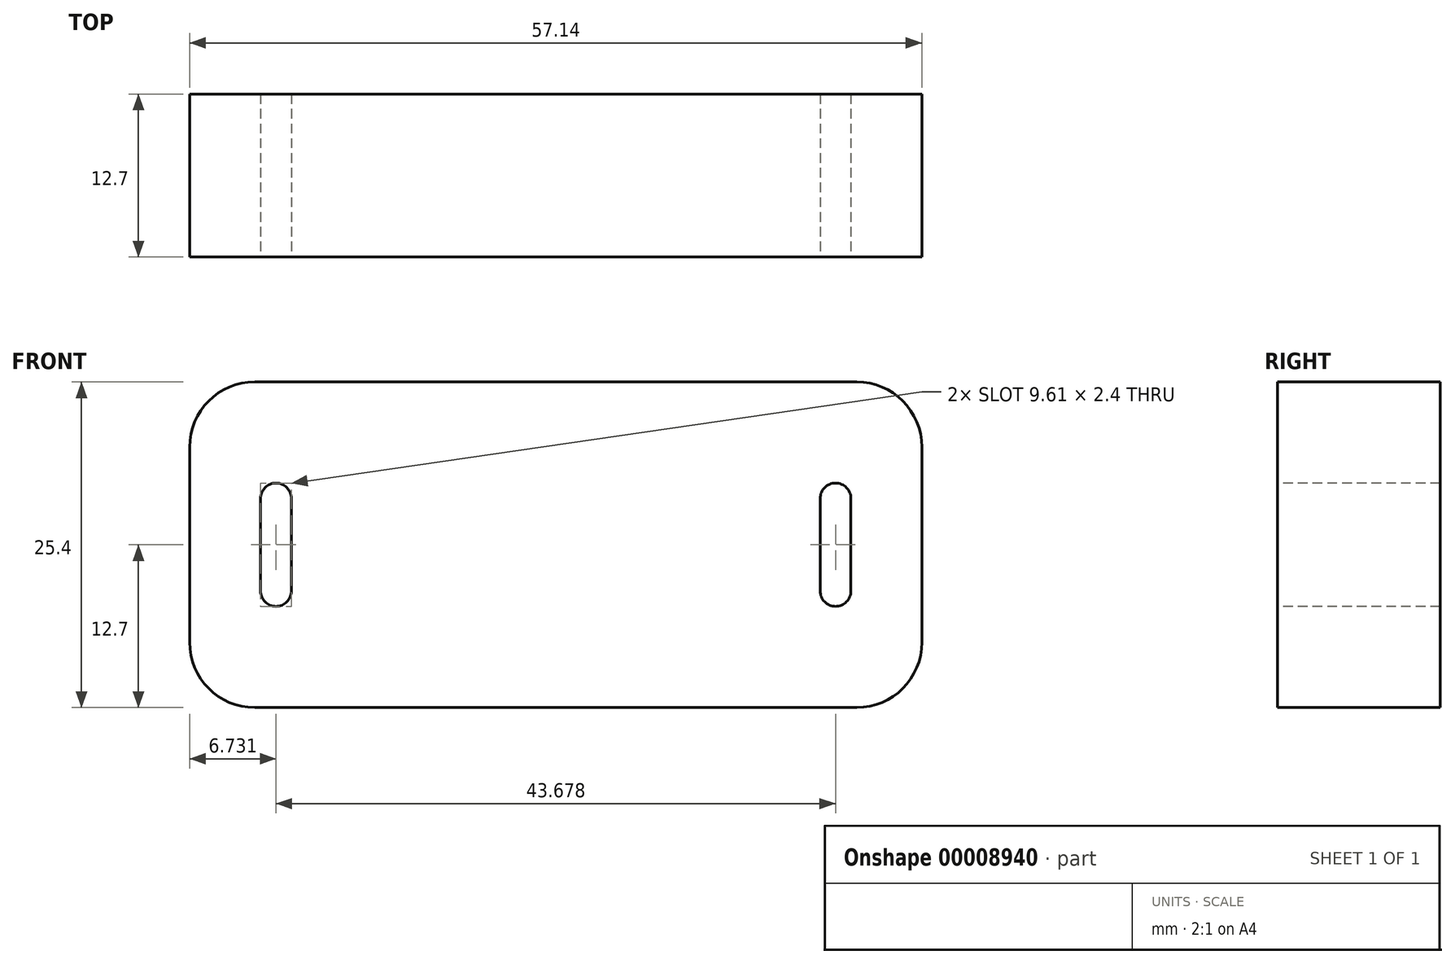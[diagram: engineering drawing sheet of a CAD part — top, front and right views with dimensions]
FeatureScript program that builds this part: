
annotation { "Feature Type Name" : "Feature", "Feature Type Description" : "" }
export const myFeature = defineFeature(function(context is Context, id is Id, definition is map)
    precondition{}
    {
        {
            var Q0;
            Q0=qCreatedBy(makeId("Top.planeOp"),FACE);
            var sketch = newSketch(context, id + "F0", { "sketchPlane" : qUnion([Q0])});
            skCircle(sketch, "E0", {"center": v(0, 0) * mm, "radius": 9.53 * mm});
            skCircle(sketch, "E1.0", {"center": v(0, 0) * mm, "radius": 12.7 * mm});
            skLineSegment(sketch, "E2", {"start": v(15.88, 9.33) * mm, "end": v(28.58, 9.33) * mm});
            skLineSegment(sketch, "E3.0", {"start": v(0, 12.5) * mm, "end": v(28.58, 12.5) * mm});
            skLineSegment(sketch, "E4", {"start": v(0, -12.7) * mm, "end": v(0, 12.5) * mm, "construction": true});
            skLineSegment(sketch, "E5", {"start": v(28.58, 9.33) * mm, "end": v(28.58, 12.5) * mm});
            skLineSegment(sketch, "E6.0.MirrorCS", {"start": v(-15.88, 9.33) * mm, "end": v(-28.58, 9.33) * mm});
            skLineSegment(sketch, "E7.0.MirrorCS", {"start": v(0, 12.5) * mm, "end": v(-28.58, 12.5) * mm});
            skLineSegment(sketch, "E8.0.MirrorCS", {"start": v(-28.58, 9.33) * mm, "end": v(-28.58, 12.5) * mm});
            skLineSegment(sketch, "E9", {"start": v(12.7, 0) * mm, "end": v(12.7, 6.16) * mm});
            skLineSegment(sketch, "E10.0.MirrorCS", {"start": v(-12.7, 0) * mm, "end": v(-12.7, 6.16) * mm});
            skPoint(sketch, "E11.newPointA", {"position": v(-12.7, 12.5) * mm});
            skPoint(sketch, "E11.newPointB", {"position": v(0, 9.33) * mm});
            skArc(sketch, "E11.filletArc", {"start": v(-12.7, 6.16) * mm, "mid": v(-13.63, 8.4) * mm, "end": v(-15.88, 9.33) * mm});
            skPoint(sketch, "E12.newPointA", {"position": v(12.7, 12.5) * mm});
            skArc(sketch, "E12.filletArc", {"start": v(15.88, 9.33) * mm, "mid": v(13.63, 8.4) * mm, "end": v(12.7, 6.16) * mm});
            skSolve(sketch);
        }
        {
            var Q0;
            Q0=makeQuery(id+"F0.imprint","IMPRINT",FACE,{"disambiguationData":[TD([[makeQuery(id+"F0.imprint","IMPRINT",EDGE,{"derivedFrom":sQuery(id+"F0.wireOp",EDGE,"E6.0.MirrorCS")}),-1.0]])]});
            var Q1;
            Q1=makeQuery(id+"F0.imprint","IMPRINT",FACE,{"disambiguationData":[TD([[makeQuery(id+"F0.imprint","IMPRINT",EDGE,{"derivedFrom":sQuery(id+"F0.wireOp",EDGE,"E0")}),-1.0]])]});
            var Q2;
            Q2=makeQuery(id+"F0.imprint","IMPRINT",FACE,{"disambiguationData":[TD([[makeQuery(id+"F0.imprint","IMPRINT",EDGE,{"derivedFrom":sQuery(id+"F0.wireOp",EDGE,"E2")}),1.0]])]});
            extrude(context, id + "F1", {"entities" : qUnion([Q0, Q1, Q2]), "depth" : 25.4 * mm});
        }
        {
            var Q0;
            Q0=makeQuery(id+"F1.opExtrude","SWEPT_FACE",FACE,{"disambiguationData":[OSD([sQuery(id+"F0.wireOp",EDGE,"E6.0.MirrorCS")])]});
            var sketch = newSketch(context, id + "F2", { "sketchPlane" : qUnion([Q0])});
            skLineSegment(sketch, "E13.0", {"start": v(-23.04, 16.3) * mm, "end": v(-23.04, 9.1) * mm});
            skLineSegment(sketch, "E14.0", {"start": v(-20.64, 16.3) * mm, "end": v(-20.64, 9.1) * mm});
            skArc(sketch, "E15", {"start": v(-23.04, 9.1) * mm, "mid": v(-21.84, 7.9) * mm, "end": v(-20.64, 9.1) * mm});
            skArc(sketch, "E16", {"start": v(-20.64, 16.3) * mm, "mid": v(-21.84, 17.5) * mm, "end": v(-23.04, 16.3) * mm});
            skLineSegment(sketch, "E17.0.MirrorCS", {"start": v(20.64, 16.3) * mm, "end": v(20.64, 9.1) * mm});
            skArc(sketch, "E18.0.MirrorCS", {"start": v(20.64, 16.3) * mm, "mid": v(21.84, 17.5) * mm, "end": v(23.04, 16.3) * mm});
            skLineSegment(sketch, "E19.0.MirrorCS", {"start": v(23.04, 16.3) * mm, "end": v(23.04, 9.1) * mm});
            skArc(sketch, "E20.0.MirrorCS", {"start": v(23.04, 9.1) * mm, "mid": v(21.84, 7.9) * mm, "end": v(20.64, 9.1) * mm});
            skSolve(sketch);
        }
        {
            var Q0;
            Q0=qSketchRegion(id+"F2",true);
            extrude(context, id + "F3", {"entities" : qUnion([Q0]), "operationType" : NewBodyOperationType.REMOVE, "oppositeDirection" : true, "depth" : 25.4 * mm});
        }
        {
            var Q0;
            Q0=makeQuery(id+"F1.opExtrude","CAP_EDGE",EDGE,{"disambiguationData":[OSD([sQuery(id+"F0.wireOp",EDGE,"E8.0.MirrorCS")])],"isStart":false});
            var Q1;
            Q1=makeQuery(id+"F1.opExtrude","CAP_EDGE",EDGE,{"disambiguationData":[OSD([sQuery(id+"F0.wireOp",EDGE,"E5")])],"isStart":false});
            var Q2;
            Q2=makeQuery(id+"F1.opExtrude","CAP_EDGE",EDGE,{"disambiguationData":[OSD([sQuery(id+"F0.wireOp",EDGE,"E5")])],"isStart":true});
            var Q3;
            Q3=makeQuery(id+"F1.opExtrude","CAP_EDGE",EDGE,{"disambiguationData":[OSD([sQuery(id+"F0.wireOp",EDGE,"E8.0.MirrorCS")])],"isStart":true});
            fillet(context, id + "F4", {"entities" : qUnion([Q0, Q1, Q2, Q3]), "radius" : 5.08 * mm, "tangentPropagation" : true, "allowEdgeOverflow" : false});
        }
        {
            var Q0;
            Q0=makeQuery(id+"F1.opExtrude","SWEPT_FACE",FACE,{"disambiguationData":[OSD([sQuery(id+"F0.wireOp",EDGE,"E3.0"),sQuery(id+"F0.wireOp",EDGE,"E7.0.MirrorCS")])]});
            var sketch = newSketch(context, id + "F5", { "sketchPlane" : qUnion([Q0])});
            skSolve(sketch);
        }
        {
            var Q0;
            {var subQ1=sQuery(id+"F0.wireOp",EDGE,"E3.0");var subQ5=sQuery(id+"F0.wireOp",EDGE,"E5");Q0=makeQuery(id+"F5.imprint","IMPRINT",FACE,{"disambiguationData":[TD([[makeQuery(id+"F5.imprint","IMPRINT",EDGE,{"derivedFrom":makeQuery(id+"F1.opExtrude","SWEPT_EDGE",EDGE,{"disambiguationData":[OSD([subQ1,subQ5])]})}),1.0]])]});}
            extrude(context, id + "F6", {"entities" : qUnion([Q0]), "depth" : 12.7 * mm});
        }
        {
            var Q0;
            Q0=makeQuery(id+"F1.opExtrude","SWEPT_BODY",BODY,{"disambiguationData":[OSD([sQuery(id+"F0.wireOp",EDGE,"E0"),sQuery(id+"F0.wireOp",EDGE,"E1.0"),sQuery(id+"F0.wireOp",EDGE,"E2"),sQuery(id+"F0.wireOp",EDGE,"E3.0"),sQuery(id+"F0.wireOp",EDGE,"E5"),sQuery(id+"F0.wireOp",EDGE,"E6.0.MirrorCS"),sQuery(id+"F0.wireOp",EDGE,"E7.0.MirrorCS"),sQuery(id+"F0.wireOp",EDGE,"E8.0.MirrorCS"),sQuery(id+"F0.wireOp",EDGE,"E9"),sQuery(id+"F0.wireOp",EDGE,"E10.0.MirrorCS"),sQuery(id+"F0.wireOp",EDGE,"E11.filletArc"),sQuery(id+"F0.wireOp",EDGE,"E12.filletArc")])]});
            deleteBodies(context, id + "F7", {"entities" : qUnion([Q0])});
        }
    });
